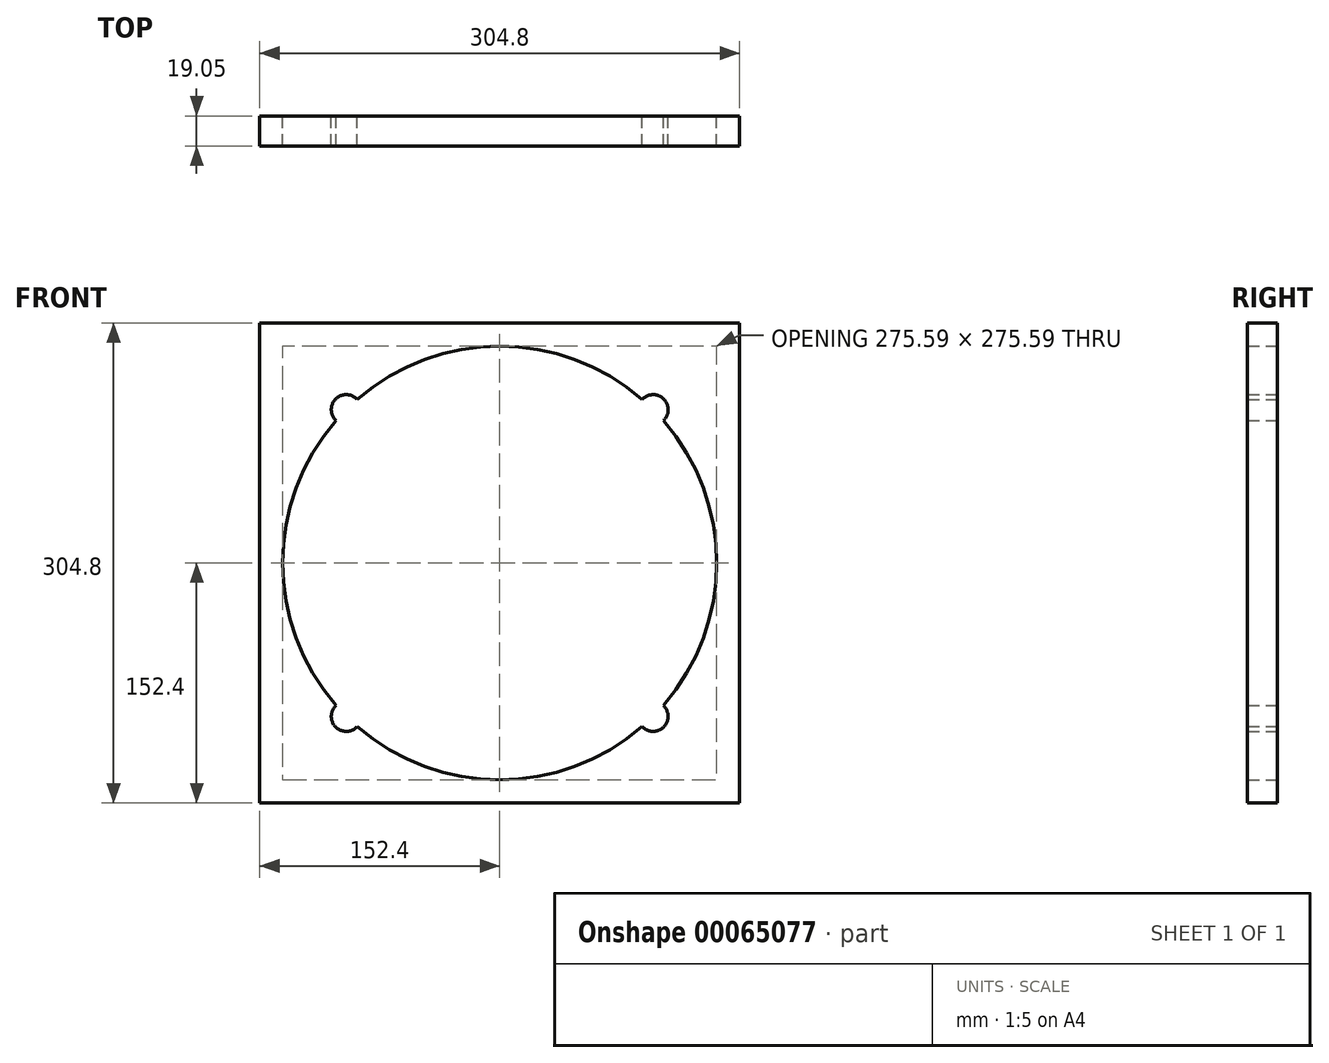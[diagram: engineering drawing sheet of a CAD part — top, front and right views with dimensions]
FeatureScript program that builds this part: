
annotation { "Feature Type Name" : "Feature", "Feature Type Description" : "" }
export const myFeature = defineFeature(function(context is Context, id is Id, definition is map)
    precondition{}
    {
        {
            var Q0;
            Q0=qCreatedBy(makeId("Front.planeOp"),FACE);
            var sketch = newSketch(context, id + "F0", { "sketchPlane" : qUnion([Q0])});
            skLineSegment(sketch, "E0.rect.bottom", {"start": v(152.4, 152.4) * mm, "end": v(-152.4, 152.4) * mm});
            skLineSegment(sketch, "E0.rect.top", {"start": v(152.4, -152.4) * mm, "end": v(-152.4, -152.4) * mm});
            skLineSegment(sketch, "E0.rect.left", {"start": v(152.4, 152.4) * mm, "end": v(152.4, -152.4) * mm});
            skLineSegment(sketch, "E0.rect.right", {"start": v(-152.4, 152.4) * mm, "end": v(-152.4, -152.4) * mm});
            skPoint(sketch, "E0.rect.middle", {"position": v(0, 0) * mm});
            skCircle(sketch, "E1", {"center": v(0, 0) * mm, "radius": 137.8 * mm});
            skCircle(sketch, "E2", {"center": v(0, 0) * mm, "radius": 128.27 * mm, "construction": true});
            skLineSegment(sketch, "E3", {"start": v(0, 0) * mm, "end": v(152.4, 152.4) * mm, "construction": true});
            skPoint(sketch, "E4", {"position": v(97.44, 97.44) * mm});
            skCircle(sketch, "E5", {"center": v(97.44, 97.44) * mm, "radius": 9.53 * mm});
            skLineSegment(sketch, "E6", {"start": v(-152.4, 152.4) * mm, "end": v(0, 0) * mm, "construction": true});
            skCircle(sketch, "E7", {"center": v(-97.44, 97.44) * mm, "radius": 9.53 * mm});
            skLineSegment(sketch, "E8", {"start": v(0, 0) * mm, "end": v(-152.4, -152.4) * mm, "construction": true});
            skLineSegment(sketch, "E9", {"start": v(0, 0) * mm, "end": v(152.4, -152.4) * mm, "construction": true});
            skCircle(sketch, "E10", {"center": v(-97.44, -97.44) * mm, "radius": 9.53 * mm});
            skCircle(sketch, "E11", {"center": v(97.44, -97.44) * mm, "radius": 9.53 * mm});
            skSolve(sketch);
        }
        {
            var Q0;
            Q0=makeQuery(id+"F0.imprint","IMPRINT",FACE,{"disambiguationData":[TD([[makeQuery(id+"F0.imprint","IMPRINT",EDGE,{"derivedFrom":sQuery(id+"F0.wireOp",EDGE,"E0.rect.bottom")}),1.0]])]});
            extrude(context, id + "F1", {"entities" : qUnion([Q0]), "depth" : 19.05 * mm});
        }
    });
